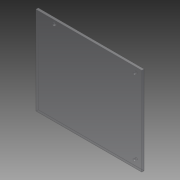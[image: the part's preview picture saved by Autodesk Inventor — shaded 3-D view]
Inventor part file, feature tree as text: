
AUTODESK INVENTOR PART (.ipt)
format: ipt  version: 2014 SP1 (Build 180222100, 222)  size: 80,896 bytes
history: native  units: in
note: dims shown in document units (in); Inventor stores cm internally (conversion verified against a paired STEP export)
features: reference x2, extrude x1, sketch x1
ambient origin geometry x8: Origin, YZ Plane, XZ Plane, XY Plane, X Axis, Y Axis, Z Axis, Center Point
bodies: Solid1 (feature_tree)
feature tree (4):
  extrude  "Extrusion1"  Depth=6.0in
  sketch  "Sketch1"  dims[d0=5.0in d1=6.0in d2=0.125in d3=0.0in d4=0.15in d5=0.25in d6=1.0in]
  reference  "Reference1"
  reference  "Reference2"
